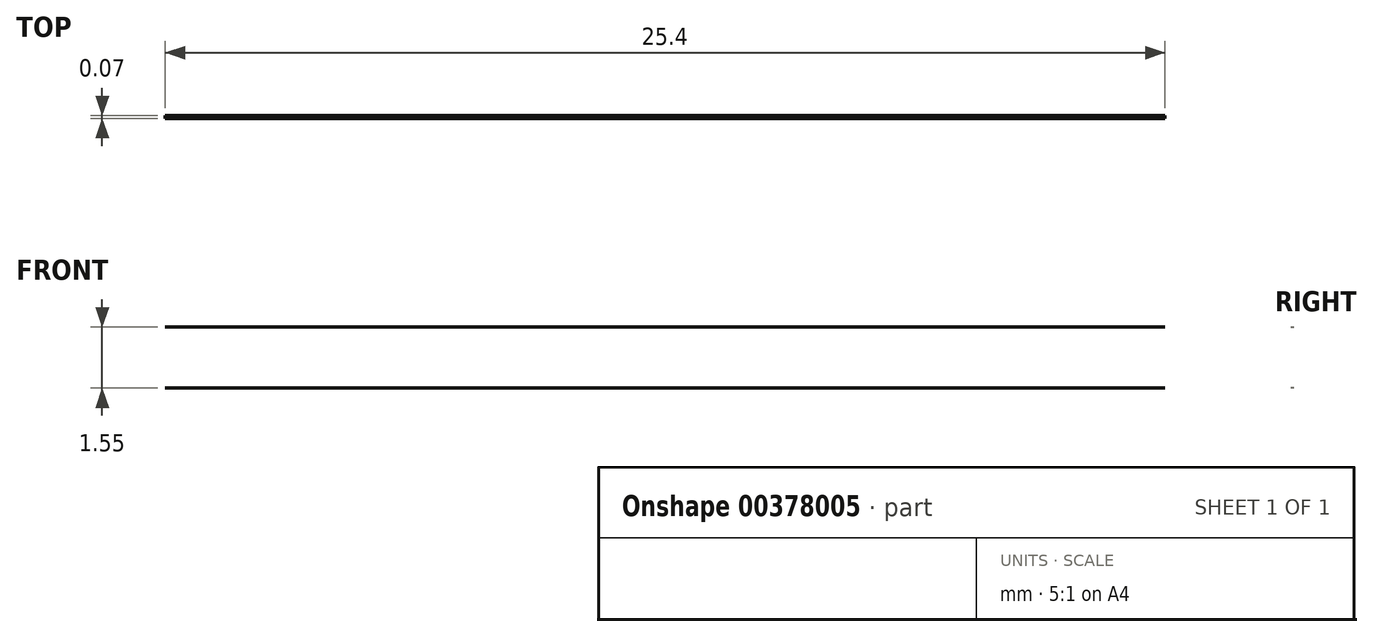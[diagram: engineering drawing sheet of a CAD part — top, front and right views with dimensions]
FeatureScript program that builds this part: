
annotation { "Feature Type Name" : "Feature", "Feature Type Description" : "" }
export const myFeature = defineFeature(function(context is Context, id is Id, definition is map)
    precondition{}
    {
        {
            var Q0;
            Q0=qCreatedBy(makeId("Right.planeOp"),FACE);
            var sketch = newSketch(context, id + "F0", { "sketchPlane" : qUnion([Q0])});
            skCircle(sketch, "E0", {"center": v(-9.28, -16.83) * mm, "radius": 3.36 * mm});
            skLineSegment(sketch, "E1.bottom", {"start": v(-7.83, -11.9) * mm, "end": v(-10.74, -11.9) * mm});
            skLineSegment(sketch, "E1.top", {"start": v(-7.83, -21.77) * mm, "end": v(-10.74, -21.77) * mm});
            skLineSegment(sketch, "E1.left", {"start": v(-4.34, -15.37) * mm, "end": v(-4.34, -18.29) * mm});
            skLineSegment(sketch, "E1.right", {"start": v(-14.22, -15.37) * mm, "end": v(-14.22, -18.29) * mm});
            skPoint(sketch, "E2.visualSharp", {"position": v(-21.98, -4.13) * mm});
            skPoint(sketch, "E3.visualSharp", {"position": v(3.42, -4.13) * mm});
            skPoint(sketch, "E4.visualSharp", {"position": v(3.42, -29.53) * mm});
            skPoint(sketch, "E5.visualSharp", {"position": v(-21.98, -29.53) * mm});
            skLineSegment(sketch, "E6.0", {"start": v(-15.28, -8.93) * mm, "end": v(-13.43, -10.78) * mm});
            skLineSegment(sketch, "E7.0", {"start": v(-17.18, -10.83) * mm, "end": v(-15.34, -12.68) * mm});
            skPoint(sketch, "E8.orphan", {"position": v(-20.44, -27.98) * mm});
            skPoint(sketch, "E9.orphan", {"position": v(-20.44, -5.68) * mm});
            skPoint(sketch, "E10.orphan", {"position": v(1.87, -5.68) * mm});
            skPoint(sketch, "E11.orphan", {"position": v(1.87, -27.98) * mm});
            skLineSegment(sketch, "E12", {"start": v(-5.13, -22.89) * mm, "end": v(-3.29, -24.73) * mm});
            skLineSegment(sketch, "E13.0", {"start": v(-5.13, -10.78) * mm, "end": v(-3.29, -8.93) * mm});
            skPoint(sketch, "E14.visualSharp", {"position": v(-20.44, -7.58) * mm});
            skArc(sketch, "E14.filletArc", {"start": v(-17.18, -10.83) * mm, "mid": v(-19.26, -10.42) * mm, "end": v(-20.44, -12.18) * mm});
            skPoint(sketch, "E15.visualSharp", {"position": v(-18.53, -5.68) * mm});
            skArc(sketch, "E15.filletArc", {"start": v(-13.93, -5.68) * mm, "mid": v(-15.7, -6.85) * mm, "end": v(-15.28, -8.93) * mm});
            skPoint(sketch, "E16.visualSharp", {"position": v(-1.93, -5.68) * mm});
            skLineSegment(sketch, "E17", {"start": v(-13.93, -5.68) * mm, "end": v(-12.17, -5.68) * mm});
            skLineSegment(sketch, "E18", {"start": v(-20.44, -12.18) * mm, "end": v(-20.44, -13.92) * mm});
            skLineSegment(sketch, "E19", {"start": v(-4.64, -27.98) * mm, "end": v(-6.37, -27.98) * mm});
            skArc(sketch, "E20.filletArc", {"start": v(-3.29, -8.93) * mm, "mid": v(-2.87, -6.85) * mm, "end": v(-4.63, -5.68) * mm});
            skPoint(sketch, "E21.visualSharp", {"position": v(1.87, -26.08) * mm});
            skPoint(sketch, "E22.visualSharp", {"position": v(-0.04, -27.98) * mm});
            skArc(sketch, "E22.filletArc", {"start": v(-4.64, -27.98) * mm, "mid": v(-2.88, -26.8) * mm, "end": v(-3.29, -24.73) * mm});
            skLineSegment(sketch, "E23.bottom", {"start": v(-1.48, -29.53) * mm, "end": v(-4.64, -29.53) * mm});
            skLineSegment(sketch, "E23.top", {"start": v(-1.5, -4.13) * mm, "end": v(-4.63, -4.13) * mm});
            skLineSegment(sketch, "E23.left", {"start": v(3.42, -24.63) * mm, "end": v(3.42, -21.48) * mm});
            skArc(sketch, "E24.filletArc", {"start": v(-0.4, -29.53) * mm, "mid": v(2.3, -28.42) * mm, "end": v(3.42, -25.72) * mm});
            skArc(sketch, "E25.filletArc", {"start": v(3.42, -7.94) * mm, "mid": v(2.3, -5.25) * mm, "end": v(-0.4, -4.13) * mm});
            skArc(sketch, "E26.filletArc", {"start": v(-18.17, -4.13) * mm, "mid": v(-20.87, -5.25) * mm, "end": v(-21.98, -7.94) * mm});
            skPoint(sketch, "E27.newPointA", {"position": v(-14.22, -21.77) * mm});
            skArc(sketch, "E27.filletArc", {"start": v(-10.74, -21.77) * mm, "mid": v(-12.2, -22.06) * mm, "end": v(-13.43, -22.89) * mm});
            skPoint(sketch, "E28.newPointA", {"position": v(-4.34, -21.77) * mm});
            skArc(sketch, "E28.filletArc", {"start": v(-5.13, -22.89) * mm, "mid": v(-6.37, -22.06) * mm, "end": v(-7.83, -21.77) * mm});
            skArc(sketch, "E29.filletArc", {"start": v(-4.34, -18.29) * mm, "mid": v(-4.05, -19.75) * mm, "end": v(-3.23, -20.98) * mm});
            skArc(sketch, "E30.filletArc", {"start": v(-3.23, -12.68) * mm, "mid": v(-4.05, -13.92) * mm, "end": v(-4.34, -15.37) * mm});
            skPoint(sketch, "E31.newPointB", {"position": v(-4.34, -11.9) * mm});
            skArc(sketch, "E31.filletArc", {"start": v(-7.83, -11.9) * mm, "mid": v(-6.37, -11.6) * mm, "end": v(-5.13, -10.78) * mm});
            skPoint(sketch, "E32.newPointB", {"position": v(-14.22, -11.9) * mm});
            skArc(sketch, "E32.filletArc", {"start": v(-13.43, -10.78) * mm, "mid": v(-12.2, -11.6) * mm, "end": v(-10.74, -11.9) * mm});
            skArc(sketch, "E33.filletArc", {"start": v(-14.22, -15.37) * mm, "mid": v(-14.51, -13.92) * mm, "end": v(-15.34, -12.68) * mm});
            skLineSegment(sketch, "E34.filletArc", {"start": v(-14.22, -18.29) * mm, "end": v(-14.22, -18.29) * mm});
            skLineSegment(sketch, "E35", {"start": v(-3.23, -20.98) * mm, "end": v(-1.38, -22.83) * mm});
            skPoint(sketch, "E36.visualSharp", {"position": v(1.87, -7.58) * mm});
            skArc(sketch, "E37.filletArc", {"start": v(-1.38, -22.83) * mm, "mid": v(0.7, -23.24) * mm, "end": v(1.87, -21.48) * mm});
            skLineSegment(sketch, "E38", {"start": v(1.87, -21.48) * mm, "end": v(1.87, -19.75) * mm});
            skLineSegment(sketch, "E39", {"start": v(-3.23, -12.68) * mm, "end": v(-1.38, -10.84) * mm});
            skArc(sketch, "E40.filletArc", {"start": v(1.87, -12.18) * mm, "mid": v(0.7, -10.42) * mm, "end": v(-1.38, -10.84) * mm});
            skArc(sketch, "E41", {"start": v(-21.98, -13.92) * mm, "mid": v(-21.2, -14.67) * mm, "end": v(-20.44, -13.92) * mm});
            skArc(sketch, "E42", {"start": v(-12.2, -5.68) * mm, "mid": v(-11.4, -4.9) * mm, "end": v(-12.2, -4.13) * mm});
            skArc(sketch, "E43", {"start": v(-6.37, -4.13) * mm, "mid": v(-7.18, -4.9) * mm, "end": v(-6.37, -5.68) * mm});
            skArc(sketch, "E44", {"start": v(1.87, -13.92) * mm, "mid": v(2.64, -14.65) * mm, "end": v(3.42, -13.92) * mm});
            skArc(sketch, "E45", {"start": v(3.42, -19.75) * mm, "mid": v(2.64, -19.03) * mm, "end": v(1.87, -19.75) * mm});
            skArc(sketch, "E46", {"start": v(-6.37, -27.98) * mm, "mid": v(-6.98, -28.76) * mm, "end": v(-6.37, -29.53) * mm});
            skArc(sketch, "E47", {"start": v(-12.2, -29.53) * mm, "mid": v(-11.44, -28.76) * mm, "end": v(-12.2, -27.98) * mm});
            skLineSegment(sketch, "E48.trimOffspring", {"start": v(-13.3, -29.53) * mm, "end": v(-17.07, -29.53) * mm});
            skLineSegment(sketch, "E49.trimOffspring", {"start": v(1.87, -13.92) * mm, "end": v(1.87, -12.18) * mm});
            skLineSegment(sketch, "E50.trimOffspring", {"start": v(3.42, -13.92) * mm, "end": v(3.42, -13.28) * mm});
            skLineSegment(sketch, "E51.trimOffspring", {"start": v(-21.98, -13.92) * mm, "end": v(-21.98, -13.28) * mm});
            skLineSegment(sketch, "E52.trimOffspring", {"start": v(-6.44, -5.68) * mm, "end": v(-4.63, -5.68) * mm});
            skLineSegment(sketch, "E53.trimOffspring", {"start": v(-12.17, -4.13) * mm, "end": v(-12.84, -4.13) * mm});
            skPoint(sketch, "E54.start.orphan", {"position": v(-12.2, -11.6) * mm});
            skPoint(sketch, "E55.start.orphan", {"position": v(-6.37, -11.6) * mm});
            skPoint(sketch, "E56.start.orphan", {"position": v(-4.05, -13.92) * mm});
            skPoint(sketch, "E57.start.orphan", {"position": v(-4.05, -19.75) * mm});
            skPoint(sketch, "E58.start.orphan", {"position": v(-14.51, -13.92) * mm});
            skPoint(sketch, "E59.start.orphan", {"position": v(-14.22, -18.29) * mm});
            skPoint(sketch, "E60.start.orphan", {"position": v(-6.37, -22.06) * mm});
            skPoint(sketch, "E61.start.orphan", {"position": v(-12.2, -22.06) * mm});
            skPoint(sketch, "E62.endSnap0", {"position": v(3.42, -10.93) * mm});
            skPoint(sketch, "E63.startSnap0", {"position": v(1.87, -20.61) * mm});
            skArc(sketch, "E64", {"start": v(-1.5, -4.13) * mm, "mid": v(-0.95, -4.63) * mm, "end": v(-0.4, -4.13) * mm});
            skArc(sketch, "E65", {"start": v(-5.73, -4.13) * mm, "mid": v(-5.18, -4.67) * mm, "end": v(-4.63, -4.13) * mm});
            skArc(sketch, "E66", {"start": v(-13.93, -4.13) * mm, "mid": v(-13.38, -4.67) * mm, "end": v(-12.84, -4.13) * mm});
            skArc(sketch, "E67", {"start": v(-18.17, -4.13) * mm, "mid": v(-17.62, -4.68) * mm, "end": v(-17.07, -4.13) * mm});
            skLineSegment(sketch, "E68", {"start": v(-21.98, -7.94) * mm, "end": v(-21.98, -9.03) * mm});
            skArc(sketch, "E69", {"start": v(-21.98, -13.28) * mm, "mid": v(-21.43, -12.73) * mm, "end": v(-21.98, -12.18) * mm});
            skArc(sketch, "E70", {"start": v(-21.98, -25.7) * mm, "mid": v(-21.55, -25.5) * mm, "end": v(-21.45, -25.03) * mm});
            skArc(sketch, "E71", {"start": v(-21.45, -25.03) * mm, "mid": v(-21.65, -24.74) * mm, "end": v(-21.98, -24.63) * mm});
            skArc(sketch, "E72", {"start": v(-17.07, -29.53) * mm, "mid": v(-17.62, -28.98) * mm, "end": v(-18.17, -29.53) * mm});
            skArc(sketch, "E73", {"start": v(-12.2, -29.53) * mm, "mid": v(-12.74, -29) * mm, "end": v(-13.3, -29.53) * mm});
            skArc(sketch, "E74", {"start": v(-4.64, -29.53) * mm, "mid": v(-5.19, -28.99) * mm, "end": v(-5.74, -29.53) * mm});
            skArc(sketch, "E75", {"start": v(-0.4, -29.53) * mm, "mid": v(-0.94, -28.99) * mm, "end": v(-1.48, -29.53) * mm});
            skLineSegment(sketch, "E76.trimOffspring", {"start": v(-13.93, -4.13) * mm, "end": v(-17.07, -4.13) * mm});
            skLineSegment(sketch, "E77.trimOffspring", {"start": v(-21.98, -12.18) * mm, "end": v(-21.98, -7.94) * mm});
            skLineSegment(sketch, "E78.trimOffspring", {"start": v(-5.74, -29.53) * mm, "end": v(-6.37, -29.53) * mm});
            skArc(sketch, "E79", {"start": v(3.42, -24.63) * mm, "mid": v(2.88, -25.18) * mm, "end": v(3.42, -25.72) * mm});
            skArc(sketch, "E80", {"start": v(3.42, -20.38) * mm, "mid": v(2.87, -20.93) * mm, "end": v(3.42, -21.48) * mm});
            skLineSegment(sketch, "E81.trimOffspring", {"start": v(3.42, -20.38) * mm, "end": v(3.42, -19.75) * mm});
            skArc(sketch, "E82", {"start": v(3.42, -7.94) * mm, "mid": v(2.87, -8.49) * mm, "end": v(3.42, -9.04) * mm});
            skArc(sketch, "E83", {"start": v(3.42, -12.18) * mm, "mid": v(2.87, -12.73) * mm, "end": v(3.42, -13.28) * mm});
            skLineSegment(sketch, "E84.trimOffspring", {"start": v(3.42, -12.18) * mm, "end": v(3.42, -9.04) * mm});
            skLineSegment(sketch, "E85.trimOffspring", {"start": v(-5.73, -4.13) * mm, "end": v(-6.44, -4.13) * mm});
            skPoint(sketch, "E86.start.orphan", {"position": v(-20.44, -19.75) * mm});
            skPoint(sketch, "E87.trimOffspring.end.orphan", {"position": v(-21.98, -19.75) * mm});
            skPoint(sketch, "E88.orphan", {"position": v(-20.44, -25.7) * mm});
            skLineSegment(sketch, "E89", {"start": v(-9.28, -16.83) * mm, "end": v(-9.28, -33.22) * mm, "construction": true});
            skArc(sketch, "E90.MirrorCS", {"start": v(-14.22, -18.29) * mm, "mid": v(-14.51, -19.75) * mm, "end": v(-15.34, -20.98) * mm});
            skLineSegment(sketch, "E91.MirrorCS", {"start": v(-15.34, -20.98) * mm, "end": v(-17.18, -22.83) * mm});
            skArc(sketch, "E92.MirrorCS", {"start": v(-17.18, -22.83) * mm, "mid": v(-19.26, -23.24) * mm, "end": v(-20.43, -21.48) * mm});
            skPoint(sketch, "E93.MirrorP", {"position": v(-20.43, -20.61) * mm});
            skArc(sketch, "E94.MirrorCS", {"start": v(-21.98, -19.75) * mm, "mid": v(-21.2, -19.03) * mm, "end": v(-20.43, -19.75) * mm});
            skLineSegment(sketch, "E95.MirrorCS", {"start": v(-20.43, -21.48) * mm, "end": v(-20.43, -19.75) * mm});
            skArc(sketch, "E96.MirrorCS", {"start": v(-21.98, -20.38) * mm, "mid": v(-21.44, -20.93) * mm, "end": v(-21.98, -21.48) * mm});
            skLineSegment(sketch, "E97.MirrorCS", {"start": v(-21.98, -20.38) * mm, "end": v(-21.98, -19.75) * mm});
            skLineSegment(sketch, "E98.MirrorCS", {"start": v(-21.98, -24.63) * mm, "end": v(-21.98, -21.48) * mm});
            skArc(sketch, "E99.MirrorCS", {"start": v(-18.17, -29.53) * mm, "mid": v(-20.87, -28.42) * mm, "end": v(-21.98, -25.72) * mm});
            skArc(sketch, "E100.MirrorCS", {"start": v(-13.93, -27.98) * mm, "mid": v(-15.7, -26.8) * mm, "end": v(-15.28, -24.73) * mm});
            skLineSegment(sketch, "E101.MirrorCS", {"start": v(-13.93, -27.98) * mm, "end": v(-12.2, -27.98) * mm});
            skPoint(sketch, "E102.orphan", {"position": v(-13.43, -22.89) * mm});
            skPoint(sketch, "E103.MirrorCS.end.orphan", {"position": v(-15.28, -24.73) * mm});
            skLineSegment(sketch, "E104.MirrorCS", {"start": v(-13.43, -22.89) * mm, "end": v(-15.28, -24.73) * mm});
            skSolve(sketch);
        }
        {
            var Q0;
            {var subQ0=sQuery(id+"F0.wireOp",EDGE,"E52.trimOffspring");var subQ1=sQuery(id+"F0.wireOp",EDGE,"E43");var subQ2=makeQuery(id+"F0.imprint","INTERSECT",VERTEX,{"disambiguationData":[OD(0.0)],"derivedFrom":[subQ1,subQ0]});Q0=makeQuery(id+"F0.imprint","IMPRINT",FACE,{"disambiguationData":[TD([[makeQuery(id+"F0.imprint","IMPRINT",EDGE,{"disambiguationData":[TD([[subQ2,1.0]])],"derivedFrom":subQ1}),1.0]])]});}
            var Q1;
            {var subQ0=sQuery(id+"F0.wireOp",EDGE,"E85.trimOffspring");var subQ1=sQuery(id+"F0.wireOp",EDGE,"E43");var subQ2=makeQuery(id+"F0.imprint","INTERSECT",VERTEX,{"disambiguationData":[OD(0.0)],"derivedFrom":[subQ1,subQ0]});Q1=makeQuery(id+"F0.imprint","IMPRINT",FACE,{"disambiguationData":[TD([[makeQuery(id+"F0.imprint","IMPRINT",EDGE,{"disambiguationData":[TD([[subQ2,-1.0]])],"derivedFrom":subQ1}),1.0]])]});}
            extrude(context, id + "F1", {"entities" : qUnion([Q0, Q1]), "depth" : 25.4 * mm});
        }
    });
